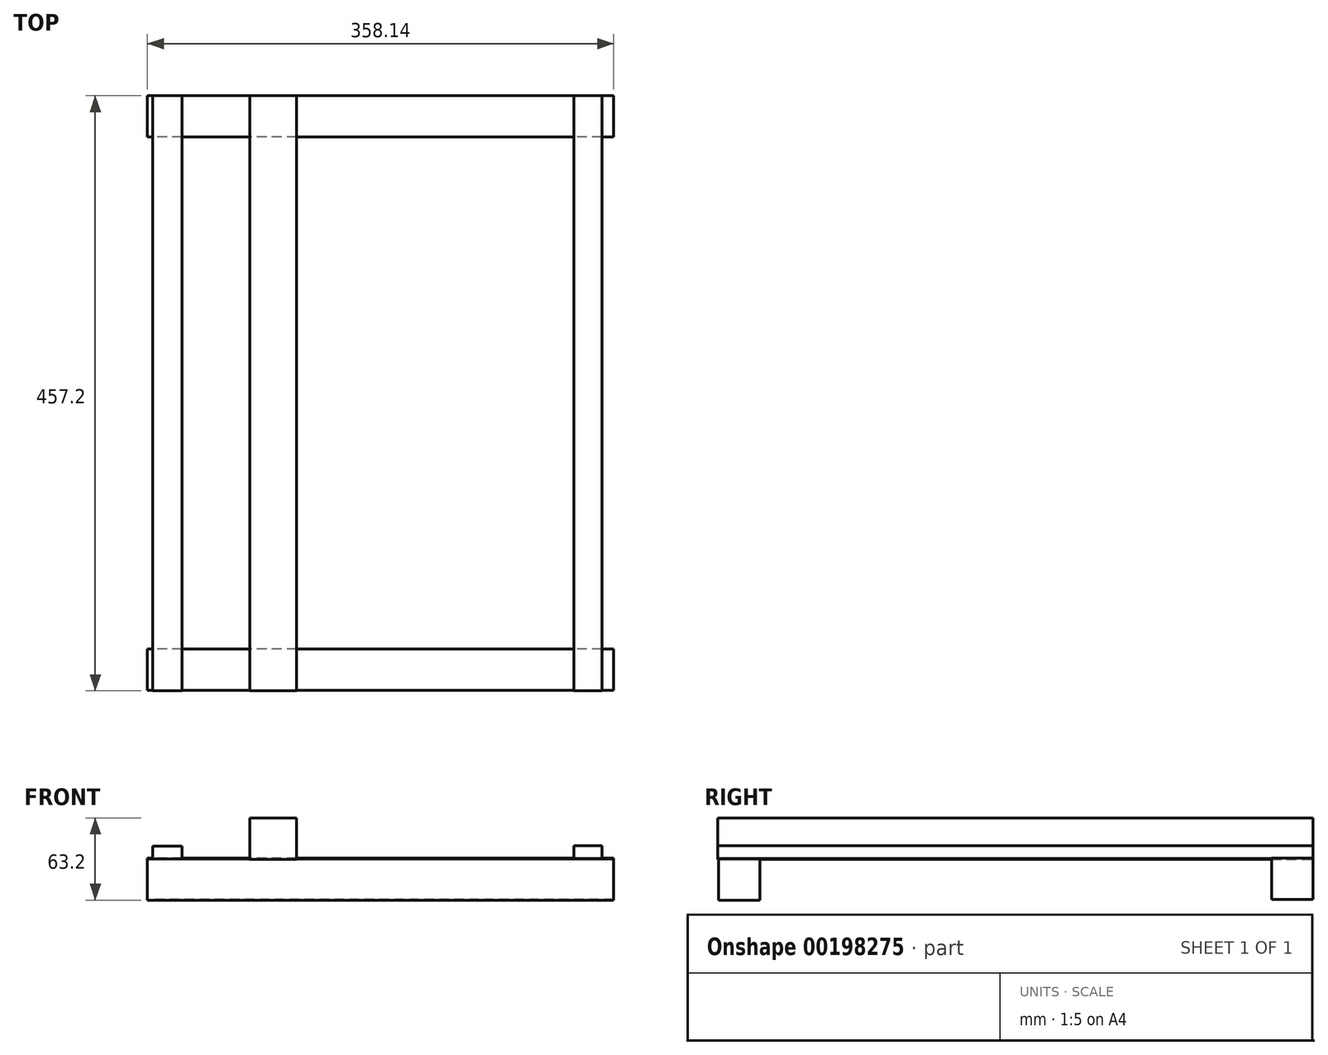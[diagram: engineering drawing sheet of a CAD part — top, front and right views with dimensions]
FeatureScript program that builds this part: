
annotation { "Feature Type Name" : "Feature", "Feature Type Description" : "" }
export const myFeature = defineFeature(function(context is Context, id is Id, definition is map)
    precondition{}
    {
        {
            var Q0;
            Q0=qCreatedBy(makeId("Right.planeOp"),FACE);
            var sketch = newSketch(context, id + "F0", { "sketchPlane" : qUnion([Q0])});
            skLineSegment(sketch, "E0.bottom", {"start": v(-228.1, -41.69) * mm, "end": v(-196.35, -41.69) * mm});
            skLineSegment(sketch, "E0.top", {"start": v(-228.1, -9.94) * mm, "end": v(-196.35, -9.94) * mm});
            skLineSegment(sketch, "E0.left", {"start": v(-228.1, -41.69) * mm, "end": v(-228.1, -9.94) * mm});
            skLineSegment(sketch, "E0.right", {"start": v(-196.35, -41.69) * mm, "end": v(-196.35, -9.94) * mm});
            skLineSegment(sketch, "E1.bottom", {"start": v(196.85, -41.2) * mm, "end": v(228.6, -41.2) * mm});
            skLineSegment(sketch, "E1.top", {"start": v(196.85, -9.44) * mm, "end": v(228.6, -9.44) * mm});
            skLineSegment(sketch, "E1.left", {"start": v(196.85, -41.2) * mm, "end": v(196.85, -9.44) * mm});
            skLineSegment(sketch, "E1.right", {"start": v(228.6, -41.2) * mm, "end": v(228.6, -9.44) * mm});
            skSolve(sketch);
        }
        {
            var Q0;
            Q0=makeQuery(id+"F0.imprint","IMPRINT",FACE,{"disambiguationData":[TD([[makeQuery(id+"F0.imprint","IMPRINT",EDGE,{"derivedFrom":sQuery(id+"F0.wireOp",EDGE,"E0.bottom")}),1.0]])]});
            var Q1;
            Q1=makeQuery(id+"F0.imprint","IMPRINT",FACE,{"disambiguationData":[TD([[makeQuery(id+"F0.imprint","IMPRINT",EDGE,{"derivedFrom":sQuery(id+"F0.wireOp",EDGE,"E1.bottom")}),1.0]])]});
            extrude(context, id + "F1", {"entities" : qUnion([Q0, Q1]), "endBound" : BoundingType.SYMMETRIC, "depth" : 358.14 * mm});
        }
        {
            var Q0;
            Q0=qCreatedBy(makeId("Front.planeOp"),FACE);
            var sketch = newSketch(context, id + "F2", { "sketchPlane" : qUnion([Q0])});
            skLineSegment(sketch, "E2.bottom", {"start": v(-175.06, -0.22) * mm, "end": v(-152.57, -0.22) * mm});
            skLineSegment(sketch, "E2.top", {"start": v(-175.06, -9.94) * mm, "end": v(-152.57, -9.94) * mm});
            skLineSegment(sketch, "E2.left", {"start": v(-175.06, -9.94) * mm, "end": v(-175.06, -0.22) * mm});
            skLineSegment(sketch, "E2.right", {"start": v(-152.57, -9.94) * mm, "end": v(-152.57, -0.22) * mm});
            skLineSegment(sketch, "E3.bottom", {"start": v(169.96, -9.66) * mm, "end": v(148.42, -9.66) * mm});
            skLineSegment(sketch, "E3.top", {"start": v(169.96, 0) * mm, "end": v(148.42, 0) * mm});
            skLineSegment(sketch, "E3.left", {"start": v(169.96, -9.66) * mm, "end": v(169.96, 0) * mm});
            skLineSegment(sketch, "E3.right", {"start": v(148.42, -9.66) * mm, "end": v(148.42, 0) * mm});
            skLineSegment(sketch, "E4.bottom", {"start": v(-100.32, -10.3) * mm, "end": v(-64.44, -10.3) * mm});
            skLineSegment(sketch, "E4.top", {"start": v(-100.32, 21.51) * mm, "end": v(-64.44, 21.51) * mm});
            skLineSegment(sketch, "E4.left", {"start": v(-100.32, -10.3) * mm, "end": v(-100.32, 21.51) * mm});
            skLineSegment(sketch, "E4.right", {"start": v(-64.44, -10.3) * mm, "end": v(-64.44, 21.51) * mm});
            skSolve(sketch);
        }
        {
            var Q0;
            Q0=makeQuery(id+"F2.imprint","IMPRINT",FACE,{"disambiguationData":[TD([[makeQuery(id+"F2.imprint","IMPRINT",EDGE,{"derivedFrom":sQuery(id+"F2.wireOp",EDGE,"E4.bottom")}),1.0]])]});
            var Q1;
            Q1=makeQuery(id+"F2.imprint","IMPRINT",FACE,{"disambiguationData":[TD([[makeQuery(id+"F2.imprint","IMPRINT",EDGE,{"derivedFrom":sQuery(id+"F2.wireOp",EDGE,"E2.bottom")}),-1.0]])]});
            var Q2;
            Q2=makeQuery(id+"F2.imprint","IMPRINT",FACE,{"disambiguationData":[TD([[makeQuery(id+"F2.imprint","IMPRINT",EDGE,{"derivedFrom":sQuery(id+"F2.wireOp",EDGE,"E3.bottom")}),-1.0]])]});
            extrude(context, id + "F3", {"entities" : qUnion([Q0, Q1, Q2]), "endBound" : BoundingType.SYMMETRIC, "depth" : 457.2 * mm});
        }
    });
